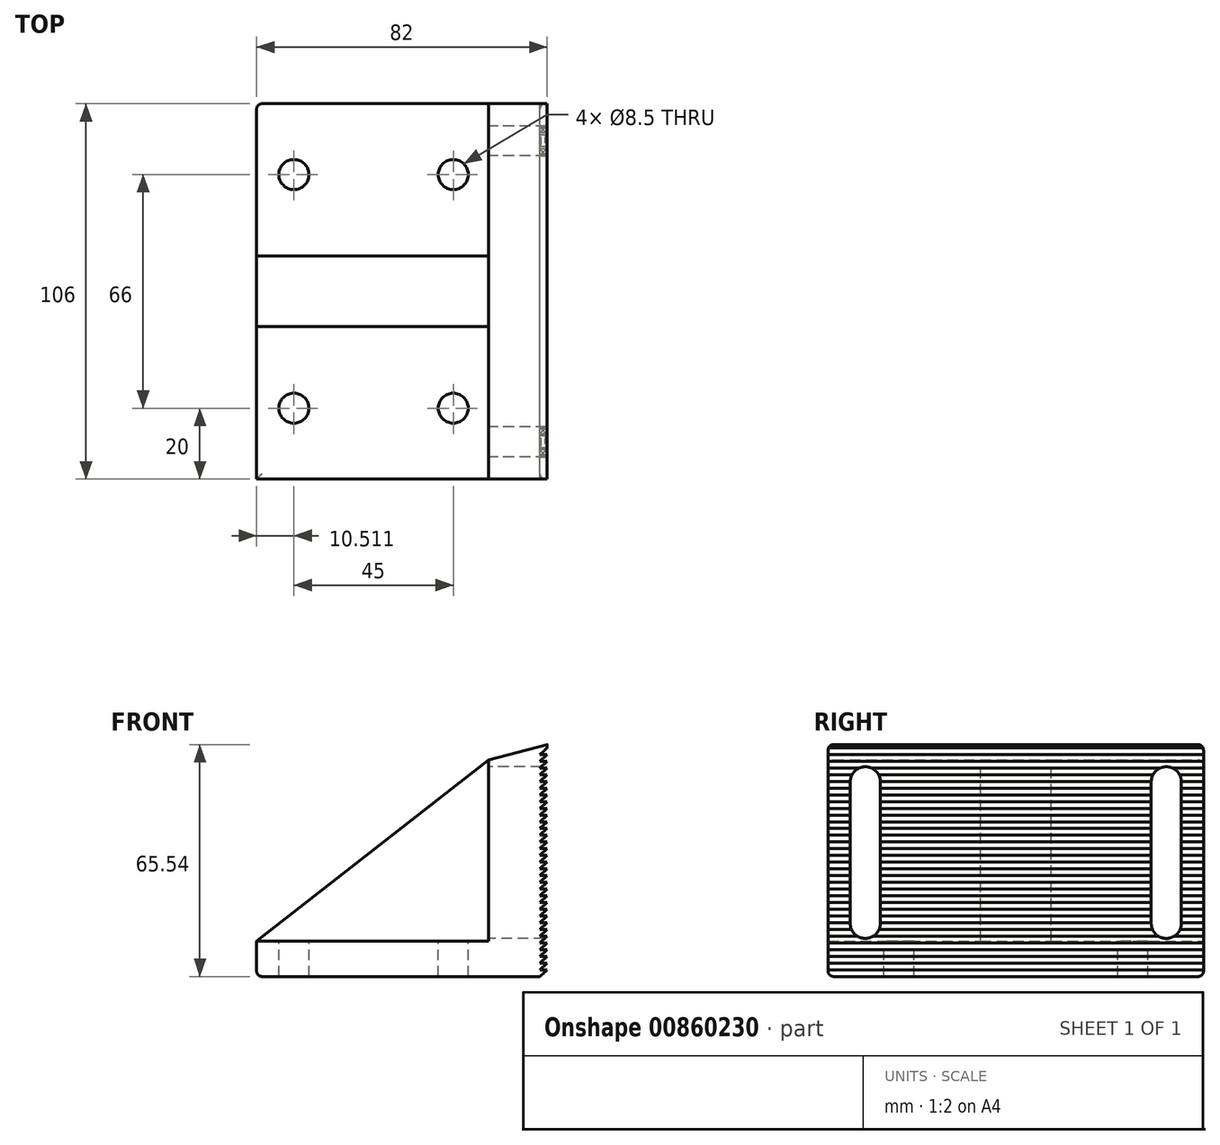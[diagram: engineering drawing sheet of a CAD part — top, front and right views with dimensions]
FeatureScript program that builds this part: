
annotation { "Feature Type Name" : "Feature", "Feature Type Description" : "" }
export const myFeature = defineFeature(function(context is Context, id is Id, definition is map)
    precondition{}
    {
        {
            var Q0;
            Q0=qCreatedBy(makeId("Front.planeOp"),FACE);
            var sketch = newSketch(context, id + "F0", { "sketchPlane" : qUnion([Q0])});
            skLineSegment(sketch, "E0", {"start": v(0, 0) * mm, "end": v(-80, 0) * mm});
            skLineSegment(sketch, "E1", {"start": v(-80, 0) * mm, "end": v(-80, 10) * mm});
            skLineSegment(sketch, "E2", {"start": v(-80, 10) * mm, "end": v(-14.49, 61.12) * mm});
            skLineSegment(sketch, "E3", {"start": v(-14.49, 61.12) * mm, "end": v(0, 65) * mm});
            skLineSegment(sketch, "E4", {"start": v(0, 0) * mm, "end": v(2, 1.9) * mm});
            skLineSegment(sketch, "E5", {"start": v(2, 1.9) * mm, "end": v(0, 1.9) * mm});
            skLineSegment(sketch, "E6", {"start": v(0, 65) * mm, "end": v(0, 0) * mm, "construction": true});
            skLineSegment(sketch, "E7", {"start": v(2, 1.9) * mm, "end": v(2, 71.6) * mm, "construction": true});
            skLineSegment(sketch, "E8", {"start": v(0, 1.9) * mm, "end": v(2, 3.8) * mm});
            skLineSegment(sketch, "E9", {"start": v(2, 3.8) * mm, "end": v(0, 3.8) * mm});
            skLineSegment(sketch, "E10", {"start": v(0, 3.8) * mm, "end": v(2, 5.7) * mm});
            skLineSegment(sketch, "E11", {"start": v(2, 5.7) * mm, "end": v(0, 5.7) * mm});
            skLineSegment(sketch, "E12", {"start": v(0, 5.7) * mm, "end": v(2, 7.6) * mm});
            skLineSegment(sketch, "E13", {"start": v(2, 7.6) * mm, "end": v(0, 7.6) * mm});
            skLineSegment(sketch, "E14", {"start": v(0, 7.6) * mm, "end": v(2, 9.5) * mm});
            skLineSegment(sketch, "E15", {"start": v(2, 9.5) * mm, "end": v(0, 9.5) * mm});
            skLineSegment(sketch, "E16", {"start": v(0, 9.5) * mm, "end": v(2, 11.4) * mm});
            skLineSegment(sketch, "E17", {"start": v(2, 11.4) * mm, "end": v(0, 11.4) * mm});
            skLineSegment(sketch, "E18", {"start": v(0, 11.4) * mm, "end": v(2, 13.3) * mm});
            skLineSegment(sketch, "E19", {"start": v(2, 13.3) * mm, "end": v(0, 13.3) * mm});
            skLineSegment(sketch, "E20", {"start": v(0, 13.3) * mm, "end": v(2, 15.2) * mm});
            skLineSegment(sketch, "E21", {"start": v(2, 15.2) * mm, "end": v(0, 15.2) * mm});
            skLineSegment(sketch, "E22", {"start": v(0, 15.2) * mm, "end": v(2, 17.1) * mm});
            skLineSegment(sketch, "E23", {"start": v(2, 17.1) * mm, "end": v(0, 17.1) * mm});
            skLineSegment(sketch, "E24", {"start": v(0, 17.1) * mm, "end": v(2, 19) * mm});
            skLineSegment(sketch, "E25", {"start": v(2, 19) * mm, "end": v(0, 19) * mm});
            skLineSegment(sketch, "E26", {"start": v(0, 19) * mm, "end": v(2, 20.9) * mm});
            skLineSegment(sketch, "E27", {"start": v(2, 20.9) * mm, "end": v(0, 20.9) * mm});
            skLineSegment(sketch, "E28", {"start": v(0, 20.9) * mm, "end": v(2, 22.8) * mm});
            skLineSegment(sketch, "E29", {"start": v(2, 22.8) * mm, "end": v(0, 22.8) * mm});
            skLineSegment(sketch, "E30", {"start": v(0, 22.8) * mm, "end": v(2, 24.7) * mm});
            skLineSegment(sketch, "E31", {"start": v(2, 24.7) * mm, "end": v(0, 24.7) * mm});
            skLineSegment(sketch, "E32", {"start": v(0, 24.7) * mm, "end": v(2, 26.6) * mm});
            skLineSegment(sketch, "E33", {"start": v(2, 26.6) * mm, "end": v(0, 26.6) * mm});
            skLineSegment(sketch, "E34", {"start": v(0, 26.6) * mm, "end": v(2, 28.5) * mm});
            skLineSegment(sketch, "E35", {"start": v(2, 28.5) * mm, "end": v(0, 28.5) * mm});
            skLineSegment(sketch, "E36", {"start": v(0, 28.5) * mm, "end": v(2, 30.4) * mm});
            skLineSegment(sketch, "E37", {"start": v(2, 30.4) * mm, "end": v(0, 30.4) * mm});
            skLineSegment(sketch, "E38", {"start": v(0, 30.4) * mm, "end": v(2, 32.3) * mm});
            skLineSegment(sketch, "E39", {"start": v(2, 32.3) * mm, "end": v(0, 32.3) * mm});
            skLineSegment(sketch, "E40", {"start": v(0, 32.3) * mm, "end": v(2, 34.2) * mm});
            skLineSegment(sketch, "E41", {"start": v(2, 34.2) * mm, "end": v(0, 34.2) * mm});
            skLineSegment(sketch, "E42", {"start": v(0, 34.2) * mm, "end": v(2, 36.1) * mm});
            skLineSegment(sketch, "E43", {"start": v(2, 36.1) * mm, "end": v(0, 36.1) * mm});
            skLineSegment(sketch, "E44", {"start": v(0, 36.1) * mm, "end": v(2, 38) * mm});
            skLineSegment(sketch, "E45", {"start": v(2, 38) * mm, "end": v(0, 38) * mm});
            skLineSegment(sketch, "E46", {"start": v(0, 38) * mm, "end": v(2, 39.9) * mm});
            skLineSegment(sketch, "E47", {"start": v(2, 39.9) * mm, "end": v(0, 39.9) * mm});
            skLineSegment(sketch, "E48", {"start": v(0, 39.9) * mm, "end": v(2, 41.8) * mm});
            skLineSegment(sketch, "E49", {"start": v(2, 41.8) * mm, "end": v(0, 41.8) * mm});
            skLineSegment(sketch, "E50", {"start": v(0, 41.8) * mm, "end": v(2, 43.7) * mm});
            skLineSegment(sketch, "E51", {"start": v(2, 43.7) * mm, "end": v(0, 43.7) * mm});
            skLineSegment(sketch, "E52", {"start": v(0, 43.7) * mm, "end": v(2, 45.6) * mm});
            skLineSegment(sketch, "E53", {"start": v(2, 45.6) * mm, "end": v(0, 45.6) * mm});
            skLineSegment(sketch, "E54", {"start": v(0, 45.6) * mm, "end": v(2, 47.5) * mm});
            skLineSegment(sketch, "E55", {"start": v(2, 47.5) * mm, "end": v(0, 47.5) * mm});
            skLineSegment(sketch, "E56", {"start": v(0, 47.5) * mm, "end": v(2, 49.4) * mm});
            skLineSegment(sketch, "E57", {"start": v(2, 49.4) * mm, "end": v(0, 49.4) * mm});
            skLineSegment(sketch, "E58", {"start": v(0, 49.4) * mm, "end": v(2, 51.3) * mm});
            skLineSegment(sketch, "E59", {"start": v(2, 51.3) * mm, "end": v(0, 51.3) * mm});
            skLineSegment(sketch, "E60", {"start": v(0, 51.3) * mm, "end": v(2, 53.2) * mm});
            skLineSegment(sketch, "E61", {"start": v(2, 53.2) * mm, "end": v(0, 53.2) * mm});
            skLineSegment(sketch, "E62", {"start": v(0, 53.2) * mm, "end": v(2, 55.1) * mm});
            skLineSegment(sketch, "E63", {"start": v(2, 55.1) * mm, "end": v(0, 55.1) * mm});
            skLineSegment(sketch, "E64", {"start": v(0, 55.1) * mm, "end": v(2, 57) * mm});
            skLineSegment(sketch, "E65", {"start": v(2, 57) * mm, "end": v(0, 57) * mm});
            skLineSegment(sketch, "E66", {"start": v(0, 57) * mm, "end": v(2, 58.9) * mm});
            skLineSegment(sketch, "E67", {"start": v(2, 58.9) * mm, "end": v(0, 58.9) * mm});
            skLineSegment(sketch, "E68", {"start": v(0, 58.9) * mm, "end": v(2, 60.8) * mm});
            skLineSegment(sketch, "E69", {"start": v(2, 60.8) * mm, "end": v(0, 60.8) * mm});
            skLineSegment(sketch, "E70", {"start": v(0, 60.8) * mm, "end": v(2, 62.7) * mm});
            skLineSegment(sketch, "E71", {"start": v(2, 62.7) * mm, "end": v(0, 62.7) * mm});
            skLineSegment(sketch, "E72", {"start": v(0, 62.7) * mm, "end": v(2, 64.6) * mm});
            skLineSegment(sketch, "E73", {"start": v(2, 64.6) * mm, "end": v(2, 65) * mm});
            skLineSegment(sketch, "E74", {"start": v(0, 65) * mm, "end": v(2, 65.54) * mm});
            skLineSegment(sketch, "E75", {"start": v(2, 65.54) * mm, "end": v(2, 65) * mm});
            skSolve(sketch);
        }
        {
            var Q0;
            Q0=makeQuery(id+"F0.imprint","IMPRINT",FACE,{"disambiguationData":[TD([[makeQuery(id+"F0.imprint","IMPRINT",EDGE,{"derivedFrom":sQuery(id+"F0.wireOp",EDGE,"E0")}),-1.0]])]});
            extrude(context, id + "F1", {"entities" : qUnion([Q0]), "depth" : 106 * mm, "offsetDistance" : 25 * mm});
        }
        {
            var Q0;
            Q0=makeQuery(id+"F1.opExtrude","CAP_FACE",FACE,{"disambiguationData":[OSD([sQuery(id+"F0.wireOp",EDGE,"E0"),sQuery(id+"F0.wireOp",EDGE,"E1"),sQuery(id+"F0.wireOp",EDGE,"E2"),sQuery(id+"F0.wireOp",EDGE,"E3"),sQuery(id+"F0.wireOp",EDGE,"E4"),sQuery(id+"F0.wireOp",EDGE,"E5"),sQuery(id+"F0.wireOp",EDGE,"E8"),sQuery(id+"F0.wireOp",EDGE,"E9"),sQuery(id+"F0.wireOp",EDGE,"E10"),sQuery(id+"F0.wireOp",EDGE,"E11"),sQuery(id+"F0.wireOp",EDGE,"E12"),sQuery(id+"F0.wireOp",EDGE,"E13"),sQuery(id+"F0.wireOp",EDGE,"E14"),sQuery(id+"F0.wireOp",EDGE,"E15"),sQuery(id+"F0.wireOp",EDGE,"E16"),sQuery(id+"F0.wireOp",EDGE,"E17"),sQuery(id+"F0.wireOp",EDGE,"E18"),sQuery(id+"F0.wireOp",EDGE,"E19"),sQuery(id+"F0.wireOp",EDGE,"E20"),sQuery(id+"F0.wireOp",EDGE,"E21"),sQuery(id+"F0.wireOp",EDGE,"E22"),sQuery(id+"F0.wireOp",EDGE,"E23"),sQuery(id+"F0.wireOp",EDGE,"E24"),sQuery(id+"F0.wireOp",EDGE,"E25"),sQuery(id+"F0.wireOp",EDGE,"E26"),sQuery(id+"F0.wireOp",EDGE,"E27"),sQuery(id+"F0.wireOp",EDGE,"E28"),sQuery(id+"F0.wireOp",EDGE,"E29"),sQuery(id+"F0.wireOp",EDGE,"E30"),sQuery(id+"F0.wireOp",EDGE,"E31"),sQuery(id+"F0.wireOp",EDGE,"E32"),sQuery(id+"F0.wireOp",EDGE,"E33"),sQuery(id+"F0.wireOp",EDGE,"E34"),sQuery(id+"F0.wireOp",EDGE,"E35"),sQuery(id+"F0.wireOp",EDGE,"E36"),sQuery(id+"F0.wireOp",EDGE,"E37"),sQuery(id+"F0.wireOp",EDGE,"E38"),sQuery(id+"F0.wireOp",EDGE,"E39"),sQuery(id+"F0.wireOp",EDGE,"E40"),sQuery(id+"F0.wireOp",EDGE,"E41"),sQuery(id+"F0.wireOp",EDGE,"E42"),sQuery(id+"F0.wireOp",EDGE,"E43"),sQuery(id+"F0.wireOp",EDGE,"E44"),sQuery(id+"F0.wireOp",EDGE,"E45"),sQuery(id+"F0.wireOp",EDGE,"E46"),sQuery(id+"F0.wireOp",EDGE,"E47"),sQuery(id+"F0.wireOp",EDGE,"E48"),sQuery(id+"F0.wireOp",EDGE,"E49"),sQuery(id+"F0.wireOp",EDGE,"E50"),sQuery(id+"F0.wireOp",EDGE,"E51"),sQuery(id+"F0.wireOp",EDGE,"E52"),sQuery(id+"F0.wireOp",EDGE,"E53"),sQuery(id+"F0.wireOp",EDGE,"E54"),sQuery(id+"F0.wireOp",EDGE,"E55"),sQuery(id+"F0.wireOp",EDGE,"E56"),sQuery(id+"F0.wireOp",EDGE,"E57"),sQuery(id+"F0.wireOp",EDGE,"E58"),sQuery(id+"F0.wireOp",EDGE,"E59"),sQuery(id+"F0.wireOp",EDGE,"E60"),sQuery(id+"F0.wireOp",EDGE,"E61"),sQuery(id+"F0.wireOp",EDGE,"E62"),sQuery(id+"F0.wireOp",EDGE,"E63"),sQuery(id+"F0.wireOp",EDGE,"E64"),sQuery(id+"F0.wireOp",EDGE,"E65"),sQuery(id+"F0.wireOp",EDGE,"E66"),sQuery(id+"F0.wireOp",EDGE,"E67"),sQuery(id+"F0.wireOp",EDGE,"E68"),sQuery(id+"F0.wireOp",EDGE,"E69"),sQuery(id+"F0.wireOp",EDGE,"E70"),sQuery(id+"F0.wireOp",EDGE,"E71"),sQuery(id+"F0.wireOp",EDGE,"E72"),sQuery(id+"F0.wireOp",EDGE,"E73"),sQuery(id+"F0.wireOp",EDGE,"E74"),sQuery(id+"F0.wireOp",EDGE,"E75")])],"isStart":false});
            var sketch = newSketch(context, id + "F2", { "sketchPlane" : qUnion([Q0])});
            skLineSegment(sketch, "E76", {"start": v(-14.49, 61.12) * mm, "end": v(-14.49, 10) * mm});
            skLineSegment(sketch, "E77", {"start": v(-14.49, 10) * mm, "end": v(-80, 10) * mm});
            skLineSegment(sketch, "E78", {"start": v(-80, 10) * mm, "end": v(-14.49, 61.12) * mm});
            skSolve(sketch);
        }
        {
            var Q0;
            Q0=makeQuery(id+"F2.imprint","IMPRINT",FACE,{"disambiguationData":[TD([[makeQuery(id+"F2.imprint","IMPRINT",EDGE,{"derivedFrom":sQuery(id+"F2.wireOp",EDGE,"E76")}),-1.0]])]});
            extrude(context, id + "F3", {"entities" : qUnion([Q0]), "operationType" : NewBodyOperationType.REMOVE, "oppositeDirection" : true, "depth" : 43 * mm, "offsetDistance" : 25 * mm});
        }
        {
            var Q0;
            Q0=makeQuery(id+"F1.opExtrude","CAP_FACE",FACE,{"disambiguationData":[OSD([sQuery(id+"F0.wireOp",EDGE,"E0"),sQuery(id+"F0.wireOp",EDGE,"E1"),sQuery(id+"F0.wireOp",EDGE,"E2"),sQuery(id+"F0.wireOp",EDGE,"E3"),sQuery(id+"F0.wireOp",EDGE,"E4"),sQuery(id+"F0.wireOp",EDGE,"E5"),sQuery(id+"F0.wireOp",EDGE,"E8"),sQuery(id+"F0.wireOp",EDGE,"E9"),sQuery(id+"F0.wireOp",EDGE,"E10"),sQuery(id+"F0.wireOp",EDGE,"E11"),sQuery(id+"F0.wireOp",EDGE,"E12"),sQuery(id+"F0.wireOp",EDGE,"E13"),sQuery(id+"F0.wireOp",EDGE,"E14"),sQuery(id+"F0.wireOp",EDGE,"E15"),sQuery(id+"F0.wireOp",EDGE,"E16"),sQuery(id+"F0.wireOp",EDGE,"E17"),sQuery(id+"F0.wireOp",EDGE,"E18"),sQuery(id+"F0.wireOp",EDGE,"E19"),sQuery(id+"F0.wireOp",EDGE,"E20"),sQuery(id+"F0.wireOp",EDGE,"E21"),sQuery(id+"F0.wireOp",EDGE,"E22"),sQuery(id+"F0.wireOp",EDGE,"E23"),sQuery(id+"F0.wireOp",EDGE,"E24"),sQuery(id+"F0.wireOp",EDGE,"E25"),sQuery(id+"F0.wireOp",EDGE,"E26"),sQuery(id+"F0.wireOp",EDGE,"E27"),sQuery(id+"F0.wireOp",EDGE,"E28"),sQuery(id+"F0.wireOp",EDGE,"E29"),sQuery(id+"F0.wireOp",EDGE,"E30"),sQuery(id+"F0.wireOp",EDGE,"E31"),sQuery(id+"F0.wireOp",EDGE,"E32"),sQuery(id+"F0.wireOp",EDGE,"E33"),sQuery(id+"F0.wireOp",EDGE,"E34"),sQuery(id+"F0.wireOp",EDGE,"E35"),sQuery(id+"F0.wireOp",EDGE,"E36"),sQuery(id+"F0.wireOp",EDGE,"E37"),sQuery(id+"F0.wireOp",EDGE,"E38"),sQuery(id+"F0.wireOp",EDGE,"E39"),sQuery(id+"F0.wireOp",EDGE,"E40"),sQuery(id+"F0.wireOp",EDGE,"E41"),sQuery(id+"F0.wireOp",EDGE,"E42"),sQuery(id+"F0.wireOp",EDGE,"E43"),sQuery(id+"F0.wireOp",EDGE,"E44"),sQuery(id+"F0.wireOp",EDGE,"E45"),sQuery(id+"F0.wireOp",EDGE,"E46"),sQuery(id+"F0.wireOp",EDGE,"E47"),sQuery(id+"F0.wireOp",EDGE,"E48"),sQuery(id+"F0.wireOp",EDGE,"E49"),sQuery(id+"F0.wireOp",EDGE,"E50"),sQuery(id+"F0.wireOp",EDGE,"E51"),sQuery(id+"F0.wireOp",EDGE,"E52"),sQuery(id+"F0.wireOp",EDGE,"E53"),sQuery(id+"F0.wireOp",EDGE,"E54"),sQuery(id+"F0.wireOp",EDGE,"E55"),sQuery(id+"F0.wireOp",EDGE,"E56"),sQuery(id+"F0.wireOp",EDGE,"E57"),sQuery(id+"F0.wireOp",EDGE,"E58"),sQuery(id+"F0.wireOp",EDGE,"E59"),sQuery(id+"F0.wireOp",EDGE,"E60"),sQuery(id+"F0.wireOp",EDGE,"E61"),sQuery(id+"F0.wireOp",EDGE,"E62"),sQuery(id+"F0.wireOp",EDGE,"E63"),sQuery(id+"F0.wireOp",EDGE,"E64"),sQuery(id+"F0.wireOp",EDGE,"E65"),sQuery(id+"F0.wireOp",EDGE,"E66"),sQuery(id+"F0.wireOp",EDGE,"E67"),sQuery(id+"F0.wireOp",EDGE,"E68"),sQuery(id+"F0.wireOp",EDGE,"E69"),sQuery(id+"F0.wireOp",EDGE,"E70"),sQuery(id+"F0.wireOp",EDGE,"E71"),sQuery(id+"F0.wireOp",EDGE,"E72"),sQuery(id+"F0.wireOp",EDGE,"E73"),sQuery(id+"F0.wireOp",EDGE,"E74"),sQuery(id+"F0.wireOp",EDGE,"E75")])],"isStart":true});
            var sketch = newSketch(context, id + "F4", { "sketchPlane" : qUnion([Q0])});
            skLineSegment(sketch, "E79", {"start": v(14.49, 61.12) * mm, "end": v(14.49, 10) * mm});
            skLineSegment(sketch, "E80", {"start": v(14.49, 10) * mm, "end": v(80, 10) * mm});
            skLineSegment(sketch, "E81", {"start": v(80, 10) * mm, "end": v(14.49, 61.12) * mm});
            skSolve(sketch);
        }
        {
            var Q0;
            Q0=makeQuery(id+"F4.imprint","IMPRINT",FACE,{"disambiguationData":[TD([[makeQuery(id+"F4.imprint","IMPRINT",EDGE,{"derivedFrom":sQuery(id+"F4.wireOp",EDGE,"E79")}),1.0]])]});
            extrude(context, id + "F5", {"entities" : qUnion([Q0]), "operationType" : NewBodyOperationType.REMOVE, "oppositeDirection" : true, "depth" : 43 * mm, "offsetDistance" : 25 * mm});
        }
        {
            var Q0;
            Q0=makeQuery(id+"F5.boolean.opBoolean","COPY",FACE,{"derivedFrom":makeQuery(id+"F5.opExtrude","SWEPT_FACE",FACE,{"disambiguationData":[OSD([sQuery(id+"F4.wireOp",EDGE,"E79")])]})});
            var sketch = newSketch(context, id + "F6", { "sketchPlane" : qUnion([Q0])});
            skLineSegment(sketch, "E82", {"start": v(10.5, 61.12) * mm, "end": v(10.5, 10) * mm, "construction": true});
            skLineSegment(sketch, "E83", {"start": v(95.5, 61.12) * mm, "end": v(95.5, 10) * mm, "construction": true});
            skCircle(sketch, "E84", {"center": v(10.5, 15) * mm, "radius": 4.25 * mm});
            skCircle(sketch, "E85", {"center": v(10.5, 55) * mm, "radius": 4.25 * mm});
            skLineSegment(sketch, "E86", {"start": v(6.25, 55) * mm, "end": v(6.25, 15) * mm});
            skLineSegment(sketch, "E87", {"start": v(14.75, 15) * mm, "end": v(14.75, 55) * mm});
            skCircle(sketch, "E88", {"center": v(95.5, 55) * mm, "radius": 4.25 * mm});
            skCircle(sketch, "E89", {"center": v(95.5, 15) * mm, "radius": 4.25 * mm});
            skLineSegment(sketch, "E90", {"start": v(91.25, 55) * mm, "end": v(91.25, 15) * mm});
            skLineSegment(sketch, "E91", {"start": v(99.75, 15) * mm, "end": v(99.75, 55) * mm});
            skSolve(sketch);
        }
        {
            var Q0;
            {var subQ0=sQuery(id+"F6.wireOp",EDGE,"E86");Q0=makeQuery(id+"F6.imprint","IMPRINT",FACE,{"disambiguationData":[TD([[makeQuery(id+"F6.imprint","IMPRINT",EDGE,{"derivedFrom":subQ0}),1.0]])]});}
            var Q1;
            {var subQ0=sQuery(id+"F6.wireOp",EDGE,"E85");var subQ1=makeQuery(id+"F6.imprint","INTERSECT",VERTEX,{"derivedFrom":[subQ0,sQuery(id+"F6.wireOp",EDGE,"E86")]});Q1=makeQuery(id+"F6.imprint","IMPRINT",FACE,{"disambiguationData":[TD([[makeQuery(id+"F6.imprint","IMPRINT",EDGE,{"disambiguationData":[TD([[subQ1,1.0]])],"derivedFrom":subQ0}),1.0]])]});}
            var Q2;
            {var subQ0=sQuery(id+"F6.wireOp",EDGE,"E84");var subQ1=makeQuery(id+"F6.imprint","INTERSECT",VERTEX,{"derivedFrom":[subQ0,sQuery(id+"F6.wireOp",EDGE,"E86")]});Q2=makeQuery(id+"F6.imprint","IMPRINT",FACE,{"disambiguationData":[TD([[makeQuery(id+"F6.imprint","IMPRINT",EDGE,{"disambiguationData":[TD([[subQ1,1.0]])],"derivedFrom":subQ0}),1.0]])]});}
            var Q3;
            {var subQ0=sQuery(id+"F6.wireOp",EDGE,"E88");var subQ1=makeQuery(id+"F6.imprint","INTERSECT",VERTEX,{"derivedFrom":[subQ0,sQuery(id+"F6.wireOp",EDGE,"E90")]});Q3=makeQuery(id+"F6.imprint","IMPRINT",FACE,{"disambiguationData":[TD([[makeQuery(id+"F6.imprint","IMPRINT",EDGE,{"disambiguationData":[TD([[subQ1,1.0]])],"derivedFrom":subQ0}),1.0]])]});}
            var Q4;
            {var subQ0=sQuery(id+"F6.wireOp",EDGE,"E90");Q4=makeQuery(id+"F6.imprint","IMPRINT",FACE,{"disambiguationData":[TD([[makeQuery(id+"F6.imprint","IMPRINT",EDGE,{"derivedFrom":subQ0}),1.0]])]});}
            var Q5;
            {var subQ0=sQuery(id+"F6.wireOp",EDGE,"E89");var subQ1=makeQuery(id+"F6.imprint","INTERSECT",VERTEX,{"derivedFrom":[subQ0,sQuery(id+"F6.wireOp",EDGE,"E90")]});Q5=makeQuery(id+"F6.imprint","IMPRINT",FACE,{"disambiguationData":[TD([[makeQuery(id+"F6.imprint","IMPRINT",EDGE,{"disambiguationData":[TD([[subQ1,1.0]])],"derivedFrom":subQ0}),1.0]])]});}
            extrude(context, id + "F7", {"entities" : qUnion([Q0, Q1, Q2, Q3, Q4, Q5]), "operationType" : NewBodyOperationType.REMOVE, "endBound" : BoundingType.THROUGH_ALL, "oppositeDirection" : true, "depth" : 25 * mm, "offsetDistance" : 25 * mm});
        }
        {
            var Q0;
            Q0=makeQuery(id+"F5.boolean.opBoolean","COPY",FACE,{"derivedFrom":makeQuery(id+"F5.opExtrude","SWEPT_FACE",FACE,{"disambiguationData":[OSD([sQuery(id+"F4.wireOp",EDGE,"E80")])]})});
            var sketch = newSketch(context, id + "F8", { "sketchPlane" : qUnion([Q0])});
            skCircle(sketch, "E92", {"center": v(-69.49, -20) * mm, "radius": 4.25 * mm});
            skCircle(sketch, "E93", {"center": v(-24.49, -20) * mm, "radius": 4.25 * mm});
            skCircle(sketch, "E94", {"center": v(-24.49, -86) * mm, "radius": 4.25 * mm});
            skCircle(sketch, "E95", {"center": v(-69.49, -86) * mm, "radius": 4.25 * mm});
            skSolve(sketch);
        }
        {
            var Q0;
            Q0=makeQuery(id+"F8.imprint","IMPRINT",FACE,{"disambiguationData":[TD([[makeQuery(id+"F8.imprint","IMPRINT",EDGE,{"derivedFrom":sQuery(id+"F8.wireOp",EDGE,"E92")}),1.0]])]});
            var Q1;
            Q1=makeQuery(id+"F8.imprint","IMPRINT",FACE,{"disambiguationData":[TD([[makeQuery(id+"F8.imprint","IMPRINT",EDGE,{"derivedFrom":sQuery(id+"F8.wireOp",EDGE,"E93")}),1.0]])]});
            var Q2;
            Q2=makeQuery(id+"F8.imprint","IMPRINT",FACE,{"disambiguationData":[TD([[makeQuery(id+"F8.imprint","IMPRINT",EDGE,{"derivedFrom":sQuery(id+"F8.wireOp",EDGE,"E94")}),1.0]])]});
            var Q3;
            Q3=makeQuery(id+"F8.imprint","IMPRINT",FACE,{"disambiguationData":[TD([[makeQuery(id+"F8.imprint","IMPRINT",EDGE,{"derivedFrom":sQuery(id+"F8.wireOp",EDGE,"E95")}),1.0]])]});
            extrude(context, id + "F9", {"entities" : qUnion([Q0, Q1, Q2, Q3]), "operationType" : NewBodyOperationType.REMOVE, "endBound" : BoundingType.THROUGH_ALL, "oppositeDirection" : true, "depth" : 25 * mm, "offsetDistance" : 25 * mm});
        }
        {
            var Q0;
            Q0=makeQuery(id+"F1.opExtrude","CAP_EDGE",EDGE,{"disambiguationData":[OSD([sQuery(id+"F0.wireOp",EDGE,"E0")])],"isStart":true});
            var Q1;
            Q1=makeQuery(id+"F1.opExtrude","SWEPT_EDGE",EDGE,{"disambiguationData":[OSD([sQuery(id+"F0.wireOp",EDGE,"E0"),sQuery(id+"F0.wireOp",EDGE,"E1")])]});
            var Q2;
            Q2=makeQuery(id+"F1.opExtrude","CAP_EDGE",EDGE,{"disambiguationData":[OSD([sQuery(id+"F0.wireOp",EDGE,"E0")])],"isStart":false});
            var Q3;
            Q3=makeQuery(id+"F5.boolean.opBoolean","COPY",EDGE,{"derivedFrom":makeQuery(id+"F5.opExtrude","CAP_EDGE",EDGE,{"disambiguationData":[OSD([sQuery(id+"F4.wireOp",EDGE,"E80")])],"isStart":true})});
            var Q4;
            Q4=makeQuery(id+"F1.opExtrude","CAP_EDGE",EDGE,{"disambiguationData":[OSD([sQuery(id+"F0.wireOp",EDGE,"E1")])],"isStart":true});
            var Q5;
            Q5=makeQuery(id+"F5.boolean.opBoolean","COPY",EDGE,{"derivedFrom":makeQuery(id+"F5.opExtrude","CAP_EDGE",EDGE,{"disambiguationData":[OSD([sQuery(id+"F4.wireOp",EDGE,"E81")])],"isStart":false})});
            var Q6;
            Q6=makeQuery(id+"F3.boolean.opBoolean","COPY",EDGE,{"derivedFrom":makeQuery(id+"F3.opExtrude","CAP_EDGE",EDGE,{"disambiguationData":[OSD([sQuery(id+"F2.wireOp",EDGE,"E78")])],"isStart":false})});
            var Q7;
            Q7=makeQuery(id+"F3.boolean.opBoolean","COPY",EDGE,{"derivedFrom":makeQuery(id+"F3.opExtrude","CAP_EDGE",EDGE,{"disambiguationData":[OSD([sQuery(id+"F2.wireOp",EDGE,"E77")])],"isStart":true})});
            var Q8;
            Q8=makeQuery(id+"F3.boolean.opBoolean","COPY",EDGE,{"derivedFrom":makeQuery(id+"F3.opExtrude","CAP_EDGE",EDGE,{"disambiguationData":[OSD([sQuery(id+"F2.wireOp",EDGE,"E76")])],"isStart":true})});
            var Q9;
            Q9=makeQuery(id+"F1.opExtrude","CAP_EDGE",EDGE,{"disambiguationData":[OSD([sQuery(id+"F0.wireOp",EDGE,"E3"),sQuery(id+"F0.wireOp",EDGE,"E74")])],"isStart":false});
            var Q10;
            Q10=makeQuery(id+"F5.boolean.opBoolean","COPY",EDGE,{"derivedFrom":makeQuery(id+"F5.opExtrude","CAP_EDGE",EDGE,{"disambiguationData":[OSD([sQuery(id+"F4.wireOp",EDGE,"E79")])],"isStart":true})});
            var Q11;
            Q11=makeQuery(id+"F1.opExtrude","CAP_EDGE",EDGE,{"disambiguationData":[OSD([sQuery(id+"F0.wireOp",EDGE,"E3"),sQuery(id+"F0.wireOp",EDGE,"E74")])],"isStart":true});
            fillet(context, id + "F10", {"entities" : qUnion([Q0, Q1, Q2, Q3, Q4, Q5, Q6, Q7, Q8, Q9, Q10, Q11]), "radius" : 1.5 * mm, "tangentPropagation" : true, "allowEdgeOverflow" : false});
        }
    });
